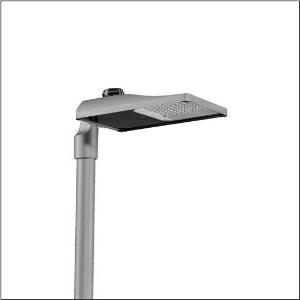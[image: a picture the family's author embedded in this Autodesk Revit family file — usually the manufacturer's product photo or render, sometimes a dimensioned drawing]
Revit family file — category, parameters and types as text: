
# Revit family: streetlight_sl_31_midi___st1_5a_5xh7p7bn08la_1a65
name_source: partatom
category: Lighting Fixtures
units: mm (PartAtom-declared; Revit-internal decimal feet)

## family parameters
Cut with Voids When Loaded = No
Host = Face
Light Source = No
Part Type = Normal
Room Calculation Point = No
Round Connector Dimension = Use Diameter
Shared = No

## types (1)
- --- (1 x LED, 10460 lm, 86.6 W, 2200K)
    Apparent Load = 87 VA
    CIE Flux Codes = 22 53 95 100 100
    Color Rendering = 70
    Color Temperature = 2200K
    Default Elevation = 1800 mm
    Description = Streetlight SL 31 midi NEMA (7pin) mast luminaire for post-top, side-entry; light control with lens of PMMA; light distribution: ST1.5a, direct asymmetric distribution, for standard-compliant lighting for roads and squares; LED: luminous flux: 10.460lm, light colour: 722, colour temperature: 2200K; luminous efficacy: 120,8lm/W; control: pre-setting: linear dimming characteristic, flexible luminous flux parameterisation, time-dependent luminous flux control, constant luminous flux control, intelligent temperature release in ECG and LED module, overheat protection; luminaire housing, of diecast aluminium, SITECO metallic grey (DB 702S), corrosivity category C5 high according to DIN EN ISO 12944; cover of toughened safety glass, transparent, opened without tools; mast flange of diecast aluminium, SITECO metallic grey (DB 702S), spigot size: 76/60mm, mast flange included unmounted; cable length: 10,5m, connection cable pre-assembled; mains connection: 220..240V, AC, 50/60Hz; power consumption (at start of service life): 86,6W / (at end of service life): 90W / (with reduced operation 50%): 39,8W; protection rating (complete): IP66; insulation class (complete): insulation class I (protective earthing); impact resistance: IK10; certification: CE, ENEC, ENEC+, VDE, UKCA; permissible operating ambient temperature for outdoor applications: -40..+50°C; packaging unit: 1 piece

Light Distribution: ST1.5a
    Height = 79 mm
    Lamp = 1 x LED
    Lamp Light Flux = 10460 lm
    Lamp Power = 86.6 W
    Lamp count = 1
    Length = 577 mm
    Luminous efficacy = 121 lm/W
    Manufacturer = Siteco
    ModVariant = No
    Model = 5XH7P7BN08LA
    Number of Poles = 1
    OnlyDefault = Yes
    Power Factor = 1
    Product Name = Streetlight SL 31 midi | ST1.5a
    Product group = mast luminaire | pylon top
    ProductGroupID = 6100
    Protection Class = Protection class I
    Protection Degree = IP 66
    RLX_Detail_Level = 1
    RLX_Emergency_Light_Flux = 0 lm
    RLX_Emergency_Type = 0
    RLX_Emergency_Type_DB = No
    RlxData = <blob elided: 29557 chars, md5=175569e7>
    Socket = socket
    Standby Power = 0 W
    System Light Flux = 10460 lm
    System Power = 87 W
    Type Comments = factory setting: luminous flux: 100 % | dim-lin: 254 | 456 mA
    Type Image = l_1300282.jpg
    URL = http://relux.com
    VarID = @adj_009813
    Voltage = 0 V
    Weight = 0.00 kg
    Width = 362 mm

## geometry (parser evidence)
native form markers: Blend x4, Sweep x11
no freeform markers — native parametric forms only
